# Revit family: IS_Contour21_S2413_BIM_DE
name_source: partatom
category: Plumbing Fixtures
revit_build: Autodesk Revit MEP 2016 (Build: 20161004_0715(x64)
units: mm (PartAtom-declared; Revit-internal decimal feet)

## family parameters
Always vertical = No
Cut with Voids When Loaded = No
OmniClass Number = 23.45.05.14.14
OmniClass Title = Sinks/Lavatories
Part Type = Normal
Room Calculation Point = No
Round Connector Dimension = Use Diameter
Shared = No
Work Plane-Based = No

## types (1)
- S241301 - CONTOUR21 handrinse washbasin 500x420mm, no taphole, no overflow
    Accessories = www.idealstandard.de\ersatzteile
    AssetType = Fixed
    BIMObjectName = ISI_IdealStandard_Wall-HungHandRinseBasins_Contour21_S241301
    BIMobject category = Basins
    BOSUseNativeGeometries = 1
    BarCode = 5017830398851
    Brand = Ideal Standard
    Brand url = http://www.idealstandard.de
    CodePerformance = DIN EN 14688 CL 00, DIN EN 31, DIN
    Color = White
    ConnectionType = Plumbing
    Cost = 0 $
    CurrencyUnit = €
    CurrentRevision = 1
    Date of publishing = 20/12/2017
    Description = IS Handwaschbecken CONTOUR 21, o.Hl., o.Ül., 500x420x195mm, Weiß
    DrainSize = 0 mm  [stored 0 ft]
    DurationUnit = Year
    EAN code = https://5017830398851
    Edition number = 1
    ExpectedLife = 25
    Features = IS Handwaschbecken CONTOUR 21, o.Hl., o.Ül., 500x420x195mm, Weiß
    Finish = White
    IFC Classification = Sanitary Terminal
    IfcExportAs = IfcSanitaryTerminalType
    Installation instructions = http://www.idealstandard.de
    InstallationInstructions = www.idealstandard.de\produkte
    MainColor = White
    MaintenanceInformation = www.idealstandard.de\produkte
    Manufacturer name = Ideal Standard
    ManufacturerURL = http://www.idealstandard.de
    Material = Vitreous china
    Material main = Ceramics
    Model = S241301
    ModelNumber = S241301
    ModelReference = IS Handwaschbecken CONTOUR 21, o.Hl., o.Ül., 500x420x195mm, Weiß
    NBS Reference Code = 35-79-93
    NBS Reference Description = Wall-Hung Hand Rinse Basins
    Name = Wall-HungHandRinseBasins_Contour21_S241301
    NettWeight = 9.61 Kg
    Nominal height = 195
    Nominal width = 500
    NominalDepth = 420 mm  [stored 1.37795 ft]
    NominalHeight = 195 mm  [stored 0.639764 ft]
    NominalLength = 420 mm  [stored 1.37795 ft]
    NominalWidth = 501 mm
    OmniClass Code = 23-31 13 00
    OmniClass Description = Sinks
    Product Guid = 9d6d3ff5-a176-4635-84b7-56878f392a23
    Product SKU = S2413
    Product data url = https://bimobject.com
    Product family = Sanitary
    Product group = Basin
    Product name = CONTOUR21 handrinse washbasin 500x420mm, no taphole, no overflow
    Product url = http://www.idealstandard.de
    ProductInformation = www.idealstandard.de/produkte
    QR code = http://bimobject.com
    Shape = Sculptured
    Size = 195 x 420 x 501mm
    Space = Internal
    SpareParts = www.idealstandard.de/ersatzteile
    Technical description = http://www.idealstandard.de
    URL = http://www.idealstandard.de
    Uniclass 1.4 Code = L7212
    Uniclass 1.4 Description = Washbasins
    Uniclass 2.0 Code = PR-35-79-93
    Uniclass 2.0 Description = Wall-Hung Hand Rinse Basins
    Uniclass 2015 Code = Pr_40_20_96_95
    Uniclass 2015 Name = Wall-hung hand rinse basins
    Uniclass2015Code = Pr_40_20_96_95
    Uniclass2015Title = Wall-hung hand rinse basins
    Uniclass2015Version = Products v1.1
    Version = 1
    VolumeUnits = Litres
    Weight Net (Kg) = 9.61

note: [stored X ft] marks values corroborated as IEEE doubles in the binary element streams (Revit-internal decimal feet)

## geometry (parser evidence)
native form markers: Blend x4, Sweep x1
no freeform markers — native parametric forms only
